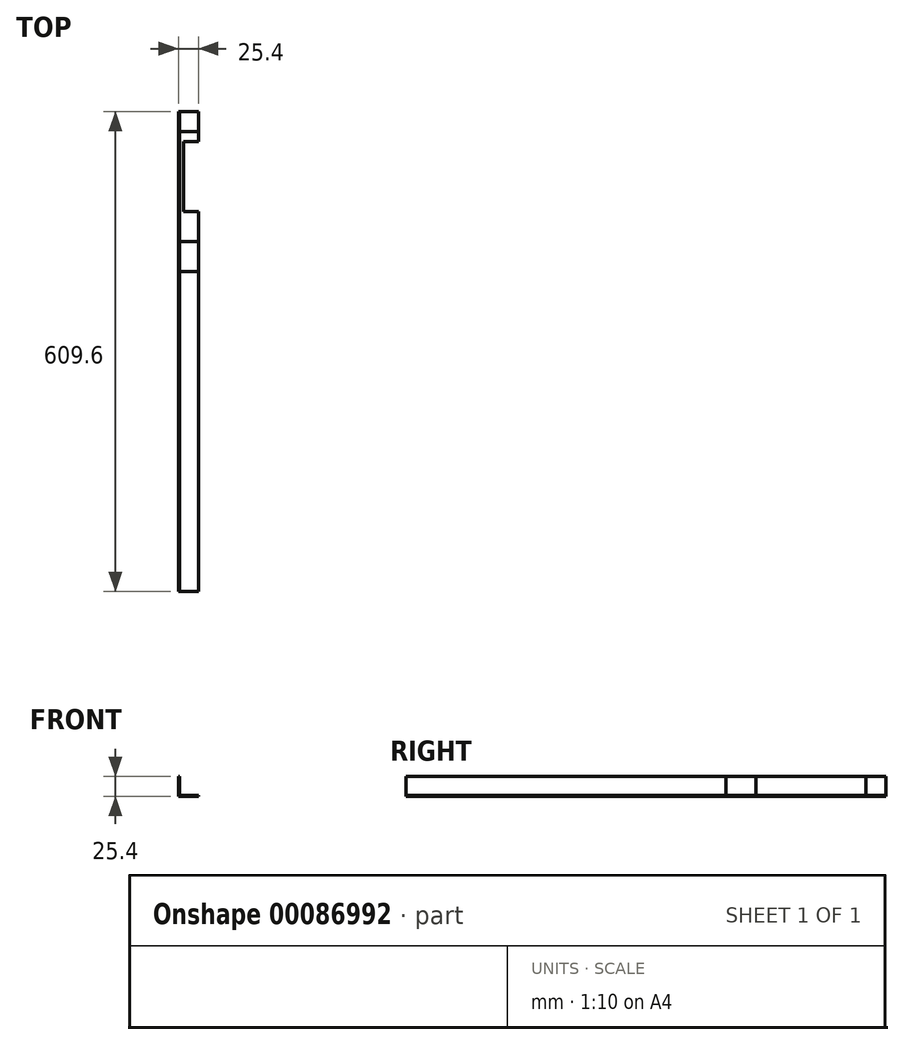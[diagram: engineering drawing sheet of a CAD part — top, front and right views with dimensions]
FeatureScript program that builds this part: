
annotation { "Feature Type Name" : "Feature", "Feature Type Description" : "" }
export const myFeature = defineFeature(function(context is Context, id is Id, definition is map)
    precondition{}
    {
        {
            var Q0;
            Q0=qCreatedBy(makeId("Front.planeOp"),FACE);
            var sketch = newSketch(context, id + "F0", { "sketchPlane" : qUnion([Q0])});
            skLineSegment(sketch, "E0", {"start": v(0, 0) * mm, "end": v(0, 25.4) * mm});
            skLineSegment(sketch, "E1", {"start": v(0, 25.4) * mm, "end": v(1.59, 25.4) * mm});
            skLineSegment(sketch, "E2", {"start": v(1.59, 25.4) * mm, "end": v(1.59, 1.59) * mm});
            skLineSegment(sketch, "E3", {"start": v(1.59, 1.59) * mm, "end": v(25.4, 1.59) * mm});
            skLineSegment(sketch, "E4", {"start": v(25.4, 1.59) * mm, "end": v(25.4, 0) * mm});
            skLineSegment(sketch, "E5", {"start": v(25.4, 0) * mm, "end": v(0, 0) * mm});
            skSolve(sketch);
        }
        {
            var Q0;
            Q0=makeQuery(id+"F0.imprint","IMPRINT",FACE,{"disambiguationData":[TD([[makeQuery(id+"F0.imprint","IMPRINT",EDGE,{"derivedFrom":sQuery(id+"F0.wireOp",EDGE,"E0")}),-1.0]])]});
            extrude(context, id + "F1", {"entities" : qUnion([Q0]), "depth" : 203.2 * mm});
        }
        {
            var Q0;
            Q0=qSketchRegion(id+"F0",true);
            extrude(context, id + "F2", {"entities" : qUnion([Q0]), "depth" : 609.6 * mm});
        }
        {
            var Q0;
            Q0=qSketchRegion(id+"F0",true);
            extrude(context, id + "F3", {"entities" : qUnion([Q0]), "depth" : 25.4 * mm});
        }
        {
            var Q0;
            Q0=qSketchRegion(id+"F0",true);
            extrude(context, id + "F4", {"entities" : qUnion([Q0]), "depth" : 165.1 * mm});
        }
        {
            var Q0;
            Q0=makeQuery(id+"F4.opExtrude","SWEPT_FACE",FACE,{"disambiguationData":[OSD([sQuery(id+"F0.wireOp",EDGE,"E3")])]});
            var sketch = newSketch(context, id + "F5", { "sketchPlane" : qUnion([Q0])});
            skLineSegment(sketch, "E6", {"start": v(25.4, -38.1) * mm, "end": v(6.35, -38.1) * mm});
            skLineSegment(sketch, "E7", {"start": v(6.35, -38.1) * mm, "end": v(6.35, -127) * mm});
            skLineSegment(sketch, "E8", {"start": v(6.35, -127) * mm, "end": v(25.4, -127) * mm});
            skLineSegment(sketch, "E9", {"start": v(25.4, -38.1) * mm, "end": v(25.4, -127) * mm});
            skSolve(sketch);
        }
        {
            var Q0;
            Q0=makeQuery(id+"F5.imprint","IMPRINT",FACE,{"disambiguationData":[TD([[makeQuery(id+"F5.imprint","IMPRINT",EDGE,{"derivedFrom":sQuery(id+"F5.wireOp",EDGE,"E6")}),1.0]])]});
            extrude(context, id + "F6", {"entities" : qUnion([Q0]), "operationType" : NewBodyOperationType.REMOVE, "oppositeDirection" : true, "depth" : 25.4 * mm});
        }
        {
            var Q0;
            Q0 = qSketchRegion(id + "F0", true);
            extrude(context, id + "F7", {"entities" : qUnion([Q0]), "depth" : 203.2 * mm});
        }
        {
            var Q0;
            Q0=makeQuery(id+"F7.opExtrude","SWEPT_BODY",BODY,{"disambiguationData":[OSD([sQuery(id+"F0.wireOp",EDGE,"E0"),sQuery(id+"F0.wireOp",EDGE,"E1"),sQuery(id+"F0.wireOp",EDGE,"E2"),sQuery(id+"F0.wireOp",EDGE,"E3"),sQuery(id+"F0.wireOp",EDGE,"E4"),sQuery(id+"F0.wireOp",EDGE,"E5")])]});
            deleteBodies(context, id + "F8", {"entities" : qUnion([Q0])});
        }
    });
